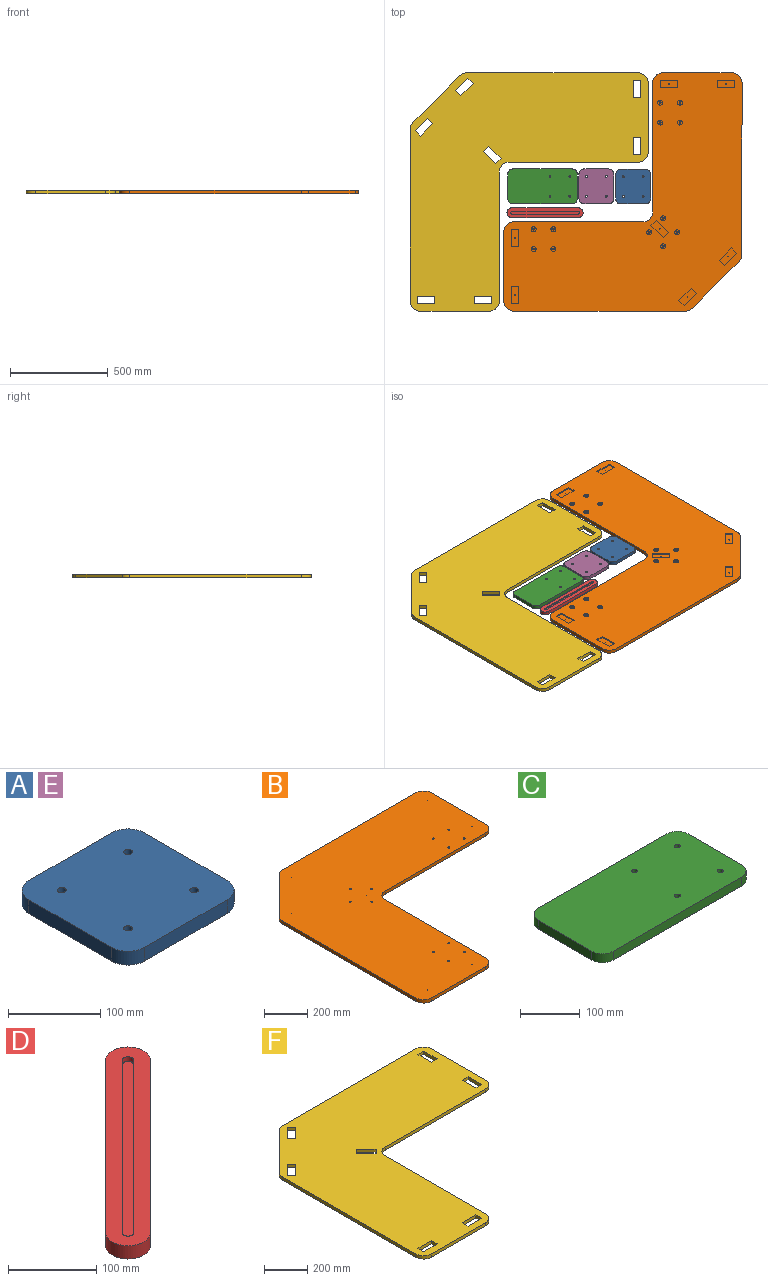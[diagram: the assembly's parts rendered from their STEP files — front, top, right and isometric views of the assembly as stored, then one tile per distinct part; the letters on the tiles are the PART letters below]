
ASSEMBLY  parts=6 mates=10
PART A: 14 faces, bbox 177.8x177.8x18.3 mm
  f0: cylinder r=25.4mm len=25.4mm, axis (0,0,-1), area 728.4mm2, adj f1,f10,f12,f13
  f1: plane 127x18.26mm, normal (-1,0,0), area 2318.5mm2, adj f0,f2,f12,f13
  f2: cylinder r=25.4mm len=25.4mm, axis (0,0,-1), area 728.4mm2, adj f1,f3,f12,f13
  f3: plane 127x18.26mm, normal (0,-1,0), area 2318.5mm2, adj f2,f4,f12,f13
  f4: cylinder r=25.4mm len=25.4mm, axis (0,0,-1), area 728.4mm2, adj f3,f5,f12,f13
  f5: plane 127x18.26mm, normal (1,0,0), area 2318.5mm2, adj f4,f6,f12,f13
  f6: cylinder r=25.4mm len=25.4mm, axis (0,0,-1), area 728.4mm2, adj f5,f10,f12,f13
  f7: cylinder r=4.76mm len=18.26mm, axis (0,0,-1), area 546.3mm2, adj f12,f13
  f8: cylinder r=4.76mm len=18.26mm, axis (0,0,-1), area 546.3mm2, adj f12,f13
  f9: cylinder r=4.76mm len=18.26mm, axis (0,0,-1), area 546.3mm2, adj f12,f13
  f10: plane 127x18.26mm, normal (0,1,0), area 2318.5mm2, adj f0,f6,f12,f13
  f11: cylinder r=4.76mm len=18.26mm, axis (0,0,-1), area 546.3mm2, adj f12,f13
  f12: plane 177.8x177.8mm, normal (0,0,1), area 30774mm2, adj f0,f1,f2,f3,f4,f5,f6,f7
  f13: plane 177.8x177.8mm, normal (0,0,-1), area 30774mm2, adj f0,f1,f2,f3,f4,f5,f6,f7
PART B: 94 faces, bbox 1219.2x1219.2x18.3 mm
  f0: plane 1219.2x1219.2mm, normal (0,0,-1), area 837946.5mm2, adj f13,f14,f15,f16,f17,f18,f20,f28
  f1: cylinder r=4.76mm len=16.86mm, axis (0,0,-1), area 504.5mm2, adj f27,f93
  f2: cylinder r=4.76mm len=16.86mm, axis (0,0,-1), area 504.5mm2, adj f27,f91
  f3: cylinder r=4.76mm len=16.86mm, axis (0,0,-1), area 504.5mm2, adj f27,f89
  f4: cylinder r=4.76mm len=16.86mm, axis (0,0,-1), area 504.5mm2, adj f27,f87
  f5: cylinder r=4.76mm len=16.86mm, axis (0,0,-1), area 504.5mm2, adj f27,f85
  f6: cylinder r=4.76mm len=16.86mm, axis (0,0,-1), area 504.5mm2, adj f27,f83
  f7: cylinder r=4.76mm len=16.86mm, axis (0,0,-1), area 504.5mm2, adj f27,f81
  f8: cylinder r=4.76mm len=16.86mm, axis (0,0,-1), area 504.5mm2, adj f27,f79
  f9: cylinder r=4.76mm len=16.86mm, axis (0,0,-1), area 504.5mm2, adj f27,f77
  f10: cylinder r=4.76mm len=16.86mm, axis (0,0,-1), area 504.5mm2, adj f27,f75
  f11: cylinder r=4.76mm len=16.86mm, axis (0,0,-1), area 504.5mm2, adj f27,f73
  f12: cylinder r=4.76mm len=16.86mm, axis (0,0,-1), area 504.5mm2, adj f27,f71
  f13: plane 239.65x239.65mm, normal (-0.71,0.71,0), area 6187.3mm2, adj f0,f27,f63,f69
  f14: plane 877.95x18.26mm, normal (-1,0,0), area 16028.1mm2, adj f0,f27,f63,f64
  f15: plane 355.6x18.26mm, normal (0,-1,0), area 6491.9mm2, adj f0,f27,f64,f65
  f16: plane 660.4x18.26mm, normal (1,0,0), area 12056.4mm2, adj f0,f27,f65,f66
  f17: plane 660.4x18.26mm, normal (0,-1,0), area 12056.4mm2, adj f0,f27,f66,f67
  f18: plane 355.6x18.26mm, normal (1,0,0), area 6491.9mm2, adj f0,f27,f67,f68
  f19: cylinder r=1.27mm len=11.91mm, axis (0,0,-1), area 95mm2, adj f27,f42
  f20: plane 877.95x18.26mm, normal (0,1,0), area 16028.1mm2, adj f0,f27,f68,f69
  f21: cylinder r=1.59mm len=11.91mm, axis (0,0,-1), area 118.8mm2, adj f27,f62
  f22: cylinder r=1.59mm len=11.91mm, axis (0,0,-1), area 118.8mm2, adj f27,f32
  f23: cylinder r=1.59mm len=11.91mm, axis (0,0,-1), area 118.8mm2, adj f27,f47
  f24: cylinder r=1.59mm len=11.91mm, axis (0,0,-1), area 118.8mm2, adj f27,f52
  f25: cylinder r=1.59mm len=11.91mm, axis (0,0,-1), area 118.8mm2, adj f27,f57
  f26: cylinder r=1.27mm len=11.91mm, axis (0,0,-1), area 95mm2, adj f27,f37
  f27: plane 1219.2x1219.2mm, normal (0,0,1), area 866837.1mm2, adj f1,f2,f3,f4,f5,f6,f7,f8
  f28: plane 38.1x6.35mm, normal (-1,0,0), area 241.9mm2, adj f0,f29,f31,f32
  f29: plane 88.9x6.35mm, normal (0,-1,0), area 564.5mm2, adj f0,f28,f30,f32
  f30: plane 38.1x6.35mm, normal (1,0,0), area 241.9mm2, adj f0,f29,f31,f32
  f31: plane 88.9x6.35mm, normal (0,1,0), area 564.5mm2, adj f0,f28,f30,f32
  f32: plane 88.9x38.1mm, normal (0,0,-1), area 3379.2mm2, adj f22,f28,f29,f30,f31
  f33: plane 26.94x26.94mm, normal (0.71,0.71,0), area 241.9mm2, adj f0,f34,f36,f37
  f34: plane 62.96x62.96mm, normal (-0.71,0.71,0), area 565.4mm2, adj f0,f33,f35,f37
  f35: plane 27.04x26.84mm, normal (-0.7,-0.71,0), area 241.9mm2, adj f0,f34,f36,f37
  f36: plane 62.86x62.86mm, normal (0.71,-0.71,0), area 564.5mm2, adj f0,f33,f35,f37
  f37: plane 89.9x89.8mm, normal (0,0,-1), area 3384.7mm2, adj f26,f33,f34,f35,f36
  f38: plane 26.94x26.94mm, normal (-0.71,-0.71,0), area 241.9mm2, adj f0,f39,f41,f42
  f39: plane 62.86x62.86mm, normal (0.71,-0.71,0), area 564.5mm2, adj f0,f38,f40,f42
  f40: plane 27.04x26.84mm, normal (0.71,0.7,0), area 241.9mm2, adj f0,f39,f41,f42
  f41: plane 62.96x62.96mm, normal (-0.71,0.71,0), area 565.4mm2, adj f0,f38,f40,f42
  f42: plane 89.9x89.8mm, normal (0,0,-1), area 3384.7mm2, adj f19,f38,f39,f40,f41
  f43: plane 38.1x6.35mm, normal (0,1,0), area 241.9mm2, adj f0,f44,f46,f47
  f44: plane 88.9x6.35mm, normal (-1,0,0), area 564.5mm2, adj f0,f43,f45,f47
  f45: plane 38.1x6.35mm, normal (0,-1,0), area 241.9mm2, adj f0,f44,f46,f47
  f46: plane 88.9x6.35mm, normal (1,0,0), area 564.5mm2, adj f0,f43,f45,f47
  f47: plane 88.9x38.1mm, normal (0,0,-1), area 3379.2mm2, adj f23,f43,f44,f45,f46
  f48: plane 88.9x6.35mm, normal (-1,0,0), area 564.5mm2, adj f0,f49,f51,f52
  f49: plane 38.1x6.35mm, normal (0,-1,0), area 241.9mm2, adj f0,f48,f50,f52
  f50: plane 88.9x6.35mm, normal (1,0,0), area 564.5mm2, adj f0,f49,f51,f52
  f51: plane 38.1x6.35mm, normal (0,1,0), area 241.9mm2, adj f0,f48,f50,f52
  f52: plane 88.9x38.1mm, normal (0,0,-1), area 3379.2mm2, adj f24,f48,f49,f50,f51
  f53: plane 62.86x62.86mm, normal (0.71,0.71,0), area 564.5mm2, adj f0,f54,f56,f57
  f54: plane 26.94x26.94mm, normal (-0.71,0.71,0), area 241.9mm2, adj f0,f53,f55,f57
  f55: plane 62.86x62.86mm, normal (-0.71,-0.71,0), area 564.5mm2, adj f0,f54,f56,f57
  f56: plane 26.94x26.94mm, normal (0.71,-0.71,0), area 241.9mm2, adj f0,f53,f55,f57
  f57: plane 89.8x89.8mm, normal (0,0,-1), area 3379.2mm2, adj f25,f53,f54,f55,f56
  f58: plane 38.1x6.35mm, normal (-1,0,0), area 241.9mm2, adj f0,f59,f61,f62
  f59: plane 88.9x6.35mm, normal (0,-1,0), area 564.5mm2, adj f0,f58,f60,f62
  f60: plane 38.1x6.35mm, normal (1,0,0), area 241.9mm2, adj f0,f59,f61,f62
  f61: plane 88.9x6.35mm, normal (0,1,0), area 564.5mm2, adj f0,f58,f60,f62
  f62: plane 88.9x38.1mm, normal (0,0,-1), area 3379.2mm2, adj f21,f58,f59,f60,f61
  f63: cylinder r=50.8mm len=35.92mm, axis (0,0,-1), area 728.4mm2, adj f0,f13,f14,f27
  f64: cylinder r=50.8mm len=50.8mm, axis (0,0,-1), area 1456.8mm2, adj f0,f14,f15,f27
  f65: cylinder r=50.8mm len=50.8mm, axis (0,0,-1), area 1456.8mm2, adj f0,f15,f16,f27
  f66: cylinder r=50.8mm len=50.8mm, axis (0,0,1), area 1456.8mm2, adj f0,f16,f17,f27
  f67: cylinder r=50.8mm len=50.8mm, axis (0,0,-1), area 1456.8mm2, adj f0,f17,f18,f27
  f68: cylinder r=50.8mm len=50.8mm, axis (0,0,-1), area 1456.8mm2, adj f0,f18,f20,f27
  f69: cylinder r=50.8mm len=35.92mm, axis (0,0,-1), area 728.4mm2, adj f0,f13,f20,f27
  f70: cylinder r=12.7mm len=25.4mm, axis (0,0,-1), area 111.5mm2, adj f0,f71
  f71: plane 25.4x25.4mm, normal (0,0,-1), area 435.5mm2, adj f12,f70
  f72: cylinder r=12.7mm len=25.4mm, axis (0,0,-1), area 111.5mm2, adj f0,f73
  f73: plane 25.4x25.4mm, normal (0,0,-1), area 435.5mm2, adj f11,f72
  f74: cylinder r=12.7mm len=25.4mm, axis (0,0,-1), area 111.5mm2, adj f0,f75
  f75: plane 25.4x25.4mm, normal (0,0,-1), area 435.5mm2, adj f10,f74
  f76: cylinder r=12.7mm len=25.4mm, axis (0,0,-1), area 111.5mm2, adj f0,f77
  f77: plane 25.4x25.4mm, normal (0,0,-1), area 435.5mm2, adj f9,f76
  f78: cylinder r=12.7mm len=25.4mm, axis (0,0,-1), area 111.5mm2, adj f0,f79
  f79: plane 25.4x25.4mm, normal (0,0,-1), area 435.5mm2, adj f8,f78
  f80: cylinder r=12.7mm len=25.4mm, axis (0,0,-1), area 111.5mm2, adj f0,f81
  f81: plane 25.4x25.4mm, normal (0,0,-1), area 435.5mm2, adj f7,f80
  f82: cylinder r=12.7mm len=25.4mm, axis (0,0,-1), area 111.5mm2, adj f0,f83
  f83: plane 25.4x25.4mm, normal (0,0,-1), area 435.5mm2, adj f6,f82
  f84: cylinder r=12.7mm len=25.4mm, axis (0,0,-1), area 111.5mm2, adj f0,f85
  f85: plane 25.4x25.4mm, normal (0,0,-1), area 435.5mm2, adj f5,f84
  f86: cylinder r=12.7mm len=25.4mm, axis (0,0,-1), area 111.5mm2, adj f0,f87
  f87: plane 25.4x25.4mm, normal (0,0,-1), area 435.5mm2, adj f4,f86
  f88: cylinder r=12.7mm len=25.4mm, axis (0,0,-1), area 111.5mm2, adj f0,f89
  f89: plane 25.4x25.4mm, normal (0,0,-1), area 435.5mm2, adj f3,f88
  f90: cylinder r=12.7mm len=25.4mm, axis (0,0,-1), area 111.5mm2, adj f0,f91
  f91: plane 25.4x25.4mm, normal (0,0,-1), area 435.5mm2, adj f2,f90
  f92: cylinder r=12.7mm len=25.4mm, axis (0,0,-1), area 111.5mm2, adj f0,f93
  f93: plane 25.4x25.4mm, normal (0,0,-1), area 435.5mm2, adj f1,f92
PART C: 14 faces, bbox 355.6x177.8x18.3 mm
  f0: plane 304.8x18.26mm, normal (0,-1,0), area 5564.5mm2, adj f1,f11,f12,f13
  f1: cylinder r=25.4mm len=25.4mm, axis (0,0,-1), area 728.4mm2, adj f0,f2,f12,f13
  f2: plane 127x18.26mm, normal (1,0,0), area 2318.5mm2, adj f1,f3,f12,f13
  f3: cylinder r=25.4mm len=25.4mm, axis (0,0,-1), area 728.4mm2, adj f2,f4,f12,f13
  f4: plane 304.8x18.26mm, normal (0,1,0), area 5564.5mm2, adj f3,f5,f12,f13
  f5: cylinder r=25.4mm len=25.4mm, axis (0,0,-1), area 728.4mm2, adj f4,f6,f12,f13
  f6: plane 127x18.26mm, normal (-1,0,0), area 2318.5mm2, adj f5,f11,f12,f13
  f7: cylinder r=4.76mm len=18.26mm, axis (0,0,-1), area 546.3mm2, adj f12,f13
  f8: cylinder r=4.76mm len=18.26mm, axis (0,0,-1), area 546.3mm2, adj f12,f13
  f9: cylinder r=4.76mm len=18.26mm, axis (0,0,-1), area 546.3mm2, adj f12,f13
  f10: cylinder r=4.76mm len=18.26mm, axis (0,0,-1), area 546.3mm2, adj f12,f13
  f11: cylinder r=25.4mm len=25.4mm, axis (0,0,-1), area 728.4mm2, adj f0,f6,f12,f13
  f12: plane 355.6x177.8mm, normal (0,0,1), area 62386.8mm2, adj f0,f1,f2,f3,f4,f5,f6,f7
  f13: plane 355.6x177.8mm, normal (0,0,-1), area 62386.8mm2, adj f0,f1,f2,f3,f4,f5,f6,f7
PART D: 11 faces, bbox 290.4x290.4x18.3 mm
  f0: cylinder r=6.35mm len=10.84mm, axis (0,0,-1), area 126.7mm2, adj f1,f3,f8,f10
  f1: plane 239.65x239.65mm, normal (0.71,-0.71,0), area 2152.1mm2, adj f0,f2,f8,f10
  f2: cylinder r=6.35mm len=10.84mm, axis (0,0,-1), area 126.7mm2, adj f1,f3,f8,f10
  f3: plane 239.65x239.65mm, normal (-0.71,0.71,0), area 2152.1mm2, adj f0,f2,f8,f10
  f4: plane 239.65x239.65mm, normal (0.71,-0.71,0), area 6187.3mm2, adj f5,f7,f8,f9
  f5: cylinder r=25.4mm len=43.36mm, axis (0,0,-1), area 1456.8mm2, adj f4,f6,f8,f9
  f6: plane 239.65x239.65mm, normal (-0.71,0.71,0), area 6187.3mm2, adj f5,f7,f8,f9
  f7: cylinder r=25.4mm len=43.36mm, axis (0,0,-1), area 1456.8mm2, adj f4,f6,f8,f9
  f8: plane 290.45x290.45mm, normal (0,0,1), area 14812.8mm2, adj f0,f1,f2,f3,f4,f5,f6,f7
  f9: plane 290.45x290.45mm, normal (0,0,-1), area 19243.8mm2, adj f4,f5,f6,f7
  f10: plane 252.35x252.35mm, normal (0,0,1), area 4430.9mm2, adj f0,f1,f2,f3
PART E: same geometry as A
PART F: 44 faces, bbox 1219.2x1219.2x18.3 mm
  f0: plane 38.1x18.26mm, normal (0,-1,0), area 695.6mm2, adj f1,f34,f35,f36
  f1: plane 88.9x18.26mm, normal (-1,0,0), area 1623mm2, adj f0,f2,f35,f36
  f2: plane 38.1x18.26mm, normal (0,1,0), area 695.6mm2, adj f1,f34,f35,f36
  f3: plane 27.04x26.84mm, normal (0.71,0.7,0), area 695.6mm2, adj f4,f27,f35,f36
  f4: plane 62.86x62.86mm, normal (0.71,-0.71,0), area 1623mm2, adj f3,f5,f35,f36
  f5: plane 26.94x26.94mm, normal (-0.71,-0.71,0), area 695.6mm2, adj f4,f27,f35,f36
  f6: plane 62.86x62.86mm, normal (0.71,-0.71,0), area 1623mm2, adj f7,f28,f35,f36
  f7: plane 27.04x26.84mm, normal (-0.7,-0.71,0), area 695.6mm2, adj f6,f8,f35,f36
  f8: plane 62.96x62.96mm, normal (-0.71,0.71,0), area 1625.5mm2, adj f7,f28,f35,f36
  f9: plane 62.86x62.86mm, normal (-0.71,-0.71,0), area 1623mm2, adj f10,f29,f35,f36
  f10: plane 26.94x26.94mm, normal (-0.71,0.71,0), area 695.6mm2, adj f9,f11,f35,f36
  f11: plane 62.86x62.86mm, normal (0.71,0.71,0), area 1623mm2, adj f10,f29,f35,f36
  f12: plane 877.95x18.26mm, normal (0,1,0), area 16028.1mm2, adj f35,f36,f37,f43
  f13: plane 239.65x239.65mm, normal (-0.71,0.71,0), area 6187.3mm2, adj f35,f36,f37,f38
  f14: plane 877.95x18.26mm, normal (-1,0,0), area 16028.1mm2, adj f35,f36,f38,f39
  f15: plane 355.6x18.26mm, normal (0,-1,0), area 6491.9mm2, adj f35,f36,f39,f40
  f16: plane 660.4x18.26mm, normal (1,0,0), area 12056.4mm2, adj f35,f36,f40,f41
  f17: plane 660.4x18.26mm, normal (0,-1,0), area 12056.4mm2, adj f35,f36,f41,f42
  f18: plane 88.9x18.26mm, normal (1,0,0), area 1623mm2, adj f19,f31,f35,f36
  f19: plane 38.1x18.26mm, normal (0,-1,0), area 695.6mm2, adj f18,f20,f35,f36
  f20: plane 88.9x18.26mm, normal (-1,0,0), area 1623mm2, adj f19,f31,f35,f36
  f21: plane 38.1x18.26mm, normal (1,0,0), area 695.6mm2, adj f22,f32,f35,f36
  f22: plane 88.9x18.26mm, normal (0,-1,0), area 1623mm2, adj f21,f23,f35,f36
  f23: plane 38.1x18.26mm, normal (-1,0,0), area 695.6mm2, adj f22,f32,f35,f36
  f24: plane 38.1x18.26mm, normal (1,0,0), area 695.6mm2, adj f25,f33,f35,f36
  f25: plane 88.9x18.26mm, normal (0,-1,0), area 1623mm2, adj f24,f26,f35,f36
  f26: plane 38.1x18.26mm, normal (-1,0,0), area 695.6mm2, adj f25,f33,f35,f36
  f27: plane 62.96x62.96mm, normal (-0.71,0.71,0), area 1625.5mm2, adj f3,f5,f35,f36
  f28: plane 26.94x26.94mm, normal (0.71,0.71,0), area 695.6mm2, adj f6,f8,f35,f36
  f29: plane 26.94x26.94mm, normal (0.71,-0.71,0), area 695.6mm2, adj f9,f11,f35,f36
  f30: plane 355.6x18.26mm, normal (1,0,0), area 6491.9mm2, adj f35,f36,f42,f43
  f31: plane 38.1x18.26mm, normal (0,1,0), area 695.6mm2, adj f18,f20,f35,f36
  f32: plane 88.9x18.26mm, normal (0,1,0), area 1623mm2, adj f21,f23,f35,f36
  f33: plane 88.9x18.26mm, normal (0,1,0), area 1623mm2, adj f24,f26,f35,f36
  f34: plane 88.9x18.26mm, normal (1,0,0), area 1623mm2, adj f0,f2,f35,f36
  f35: plane 1219.2x1219.2mm, normal (0,0,-1), area 844027mm2, adj f0,f1,f2,f3,f4,f5,f6,f7
  f36: plane 1219.2x1219.2mm, normal (0,0,1), area 844027mm2, adj f0,f1,f2,f3,f4,f5,f6,f7
  f37: cylinder r=50.8mm len=35.92mm, axis (0,0,1), area 728.4mm2, adj f12,f13,f35,f36
  f38: cylinder r=50.8mm len=35.92mm, axis (0,0,1), area 728.4mm2, adj f13,f14,f35,f36
  f39: cylinder r=50.8mm len=50.8mm, axis (0,0,1), area 1456.8mm2, adj f14,f15,f35,f36
  f40: cylinder r=50.8mm len=50.8mm, axis (0,0,1), area 1456.8mm2, adj f15,f16,f35,f36
  f41: cylinder r=50.8mm len=50.8mm, axis (0,0,-1), area 1456.8mm2, adj f16,f17,f35,f36
  f42: cylinder r=50.8mm len=50.8mm, axis (0,0,1), area 1456.8mm2, adj f17,f30,f35,f36
  f43: cylinder r=50.8mm len=50.8mm, axis (0,0,1), area 1456.8mm2, adj f12,f30,f35,f36
PLACE A t=(1228.58,-227.97,52.65)mm
PLACE B rot(axis=(-0.71,-0.71,0),180deg) t=(934.73,-662,920.22)mm
PLACE C t=(853.42,-226.76,70.91)mm
PLACE D rot(axis=(0,0,-1),45deg) t=(283.7,-805.18,70.91)mm
PLACE E t=(1040.03,-226.7,52.65)mm
PLACE F t=(454.46,-662,513.82)mm
MATE parallel F.f35 <-> B.f21  axis (0,0,-1) through (784.66,-604.85,495.56)mm
MATE planar F.f35 <-> B.f12  axis (0,0,-1) through (931.7,79.96,495.56)mm
MATE planar F.f15 <-> B.f14  axis (0,-1,0) through (683.06,-662,504.69)mm
MATE parallel D.f9 <-> B.f27  axis (0,0,-1) through (1145.81,-158.97,495.56)mm
MATE planar A.f12 <-> B.f0  axis (0,0,1) through (1596.88,-24.77,513.82)mm
MATE planar E.f12 <-> A.f11  axis (0,0,1) through (1408.33,-23.5,513.82)mm
MATE planar F.f36 <-> B.f0  axis (0,0,1) through (911.66,-611.2,513.82)mm
MATE planar C.f12 <-> A.f12  axis (0,0,1) through (1132.41,-23.56,513.82)mm
MATE planar D.f9 <-> B.f27  axis (0,0,-1) through (1145.81,-158.97,495.56)mm
MATE parallel D.f4 <-> B.f16  axis (0,-1,0) through (1145.81,-184.37,504.69)mm
